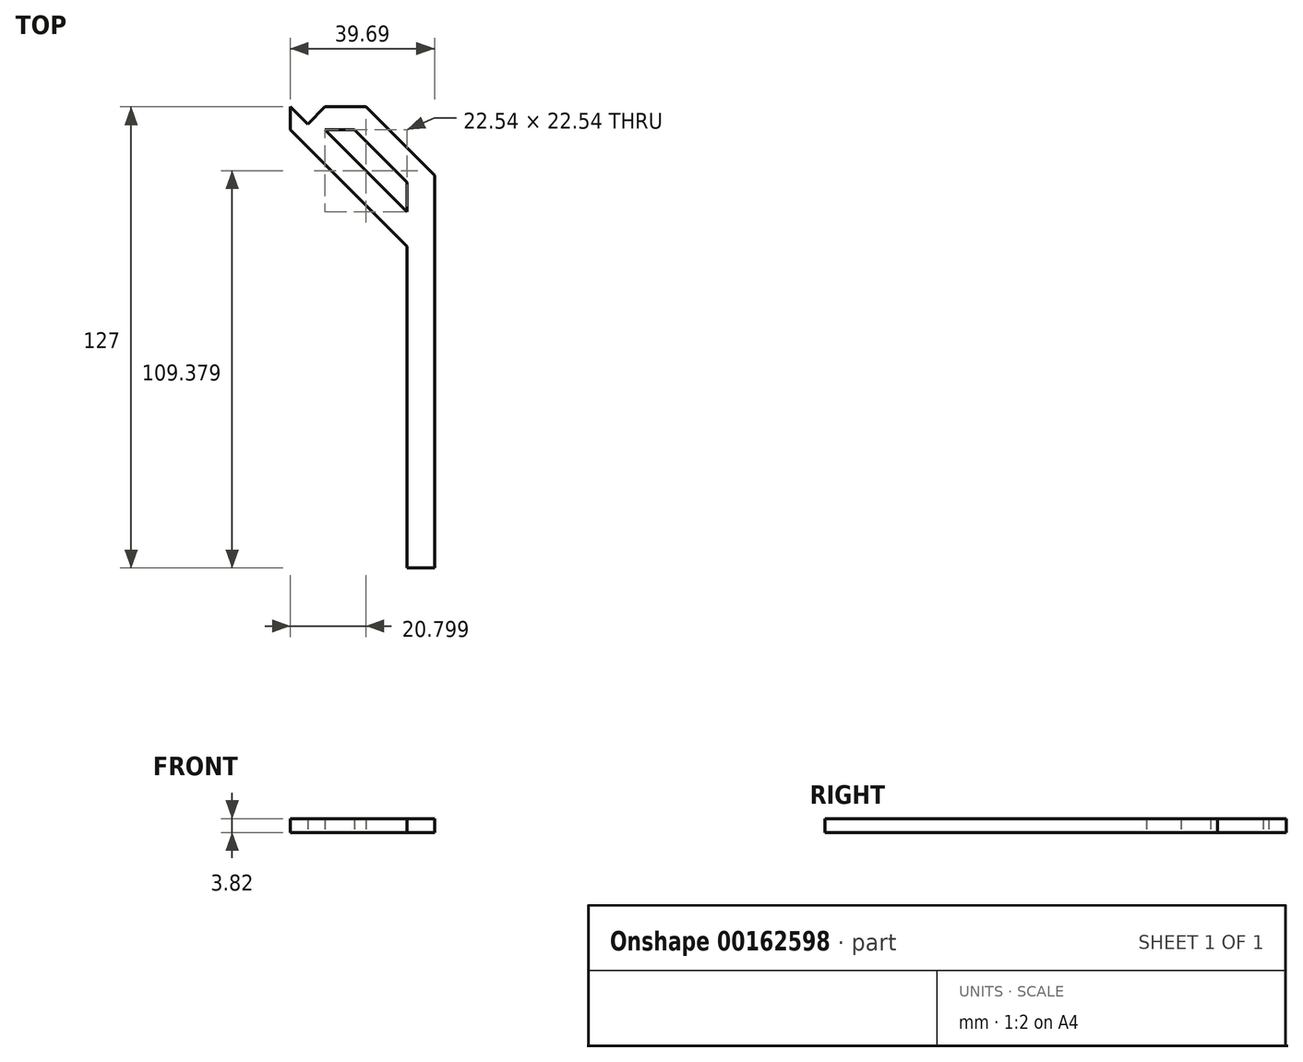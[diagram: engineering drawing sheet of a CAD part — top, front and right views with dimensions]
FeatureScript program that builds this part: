
annotation { "Feature Type Name" : "Feature", "Feature Type Description" : "" }
export const myFeature = defineFeature(function(context is Context, id is Id, definition is map)
    precondition{}
    {
        {
            var Q0;
            Q0=qCreatedBy(makeId("Top.planeOp"),FACE);
            var sketch = newSketch(context, id + "F0", { "sketchPlane" : qUnion([Q0])});
            skLineSegment(sketch, "E0", {"start": v(-3.81, 0) * mm, "end": v(3.81, 0) * mm});
            skLineSegment(sketch, "E1", {"start": v(3.81, 0) * mm, "end": v(3.81, 127) * mm});
            skLineSegment(sketch, "E2", {"start": v(-3.81, 0) * mm, "end": v(-3.81, 120.65) * mm});
            skLineSegment(sketch, "E3", {"start": v(3.81, 127) * mm, "end": v(-26.35, 127) * mm});
            skLineSegment(sketch, "E4", {"start": v(-3.8, 120.65) * mm, "end": v(-26.35, 120.65) * mm});
            skLineSegment(sketch, "E5", {"start": v(-26.35, 120.65) * mm, "end": v(-31.12, 115.89) * mm, "construction": true});
            skLineSegment(sketch, "E6", {"start": v(-31.12, 115.89) * mm, "end": v(-35.88, 120.65) * mm});
            skLineSegment(sketch, "E7", {"start": v(-26.35, 127) * mm, "end": v(-31.12, 122.24) * mm});
            skLineSegment(sketch, "E8", {"start": v(-31.12, 122.24) * mm, "end": v(-35.88, 127) * mm});
            skLineSegment(sketch, "E9", {"start": v(-35.88, 127) * mm, "end": v(-35.88, 120.65) * mm});
            skLineSegment(sketch, "E10", {"start": v(-31.12, 115.89) * mm, "end": v(-3.81, 88.58) * mm});
            skLineSegment(sketch, "E11", {"start": v(-26.35, 120.65) * mm, "end": v(-3.8, 98.1) * mm});
            skLineSegment(sketch, "E12", {"start": v(-15.08, 127) * mm, "end": v(3.81, 108.1) * mm});
            skPoint(sketch, "E12.startSnap0", {"position": v(-15.08, 120.65) * mm});
            skLineSegment(sketch, "E13", {"start": v(-18.26, 120.65) * mm, "end": v(-3.8, 106.2) * mm});
            skPoint(sketch, "E14.endSnap0", {"position": v(-28.73, 118.27) * mm});
            skLineSegment(sketch, "E15", {"start": v(-11.03, 113.43) * mm, "end": v(-6.27, 118.19) * mm, "construction": true});
            skSolve(sketch);
        }
        {
            var Q0;
            {var subQ3=sQuery(id+"F0.wireOp",EDGE,"E0");Q0=makeQuery(id+"F0.imprint","IMPRINT",FACE,{"disambiguationData":[TD([[makeQuery(id+"F0.imprint","IMPRINT",EDGE,{"derivedFrom":subQ3}),1.0]])]});}
            var Q1;
            Q1=makeQuery(id+"F0.imprint","IMPRINT",FACE,{"disambiguationData":[TD([[makeQuery(id+"F0.imprint","IMPRINT",EDGE,{"derivedFrom":sQuery(id+"F0.wireOp",EDGE,"E6")}),-1.0]])]});
            var Q2;
            {var subQ0=sQuery(id+"F0.wireOp",EDGE,"E13");Q2=makeQuery(id+"F0.imprint","IMPRINT",FACE,{"disambiguationData":[TD([[makeQuery(id+"F0.imprint","IMPRINT",EDGE,{"derivedFrom":subQ0}),1.0]])]});}
            extrude(context, id + "F1", {"entities" : qUnion([Q0, Q1, Q2]), "endBound" : BoundingType.SYMMETRIC, "depth" : 3.8 * mm});
        }
    });
